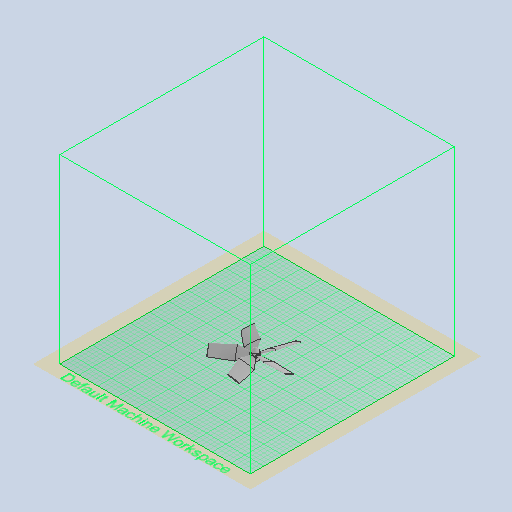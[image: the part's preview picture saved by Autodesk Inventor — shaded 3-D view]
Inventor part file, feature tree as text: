
AUTODESK INVENTOR PART (.ipt)
format: ipt  version: 2022 (Build 260153000, 153)  size: 2,093,568 bytes
history: native  units: mm
features: sketch x9, plane x4, extrude x3, fillet x3, loft x2, revolve x1, pattern_circular x1, other x1
ambient origin geometry x8: Origin, YZ Plane, XZ Plane, XY Plane, X Axis, Y Axis, Z Axis, Center Point
bodies: Solid1 (feature_tree)
feature tree (24):
  sketch  "Sketch1"  dims[d0=7.5mm d1=13.0mm]
  plane  "Work Plane1"
  plane  "Work Plane3"
  plane  "Work Plane4"
  sketch  "Sketch2"  dims[d2=7.0mm d4=1.5mm]
  sketch  "Sketch3"  dims[d5=7.0mm d6=10.0mm]
  sketch  "Sketch4"  dims[d7=4.5mm d10=7.5mm d12=15.0mm d13=30.0mm]
  sketch  "Sketch6"  dims[d14=6.5mm d15=2.5mm]
  sketch  "Sketch7"  dims[d16=9.0mm]
  revolve  "Revolution1"  [1 undecoded]
  sketch  "Sketch8"  dims[d17=1.8mm]
  plane  "Work Plane5"
  sketch  "Sketch9"  dims[d18=15.0mm]
  extrude  "Extrusion2"  Depth=1.5mm
  extrude  "Extrusion3"  Depth=10.0mm
  loft  "Loft5"
  loft  "Loft6"
  pattern_circular  "Circular Pattern3"  Angle=90.0deg  [1 undecoded]
  extrude  "Extrusion4"  Depth=9.0mm
  fillet  "Fillet3"  Radius=75.0mm
  fillet  "Fillet4"  Radius=1.0mm
  fillet  "Fillet5"  Radius=12.0mm
  sketch  "Sketch10"  dims[d19=1.6mm d37=90.0deg d38=9.0mm d43=75.0mm d44=1.0mm d45=12.0mm d50=6.0mm d51=2.0mm d61=10.0mm d62=0.0mm d63=2.0mm d64=0.0mm d65=4.0mm d70=0.0mm d71=90.0deg d72=0.0mm d73=90.0deg d74=0.0mm d75=90.0deg d76=0.0mm d77=90.0deg d78=50.0mm d79=360.0deg d81=10.0mm d82=0.0mm d83=1.0mm d84=0.4mm d85=0.4mm d66=0.0mm]
  other  "Edges3"
note: 2 required parameter values undecoded (feature->parameter linkage not recoverable at this tier; creation-order binding heuristic only, values carry confidence <= 0.55)